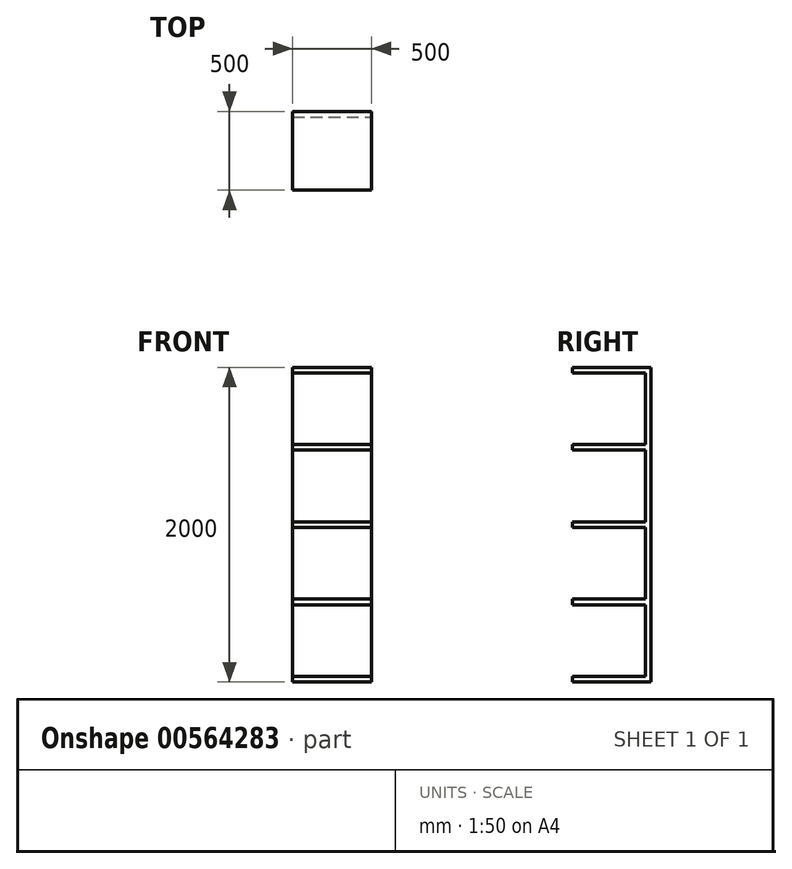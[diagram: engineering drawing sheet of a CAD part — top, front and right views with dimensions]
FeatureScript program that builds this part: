
annotation { "Feature Type Name" : "Feature", "Feature Type Description" : "" }
export const myFeature = defineFeature(function(context is Context, id is Id, definition is map)
    precondition{}
    {
        {
            var Q0;
            Q0=qCreatedBy(makeId("Front.planeOp"),FACE);
            var sketch = newSketch(context, id + "F0", { "sketchPlane" : qUnion([Q0])});
            skLineSegment(sketch, "E0.bottom", {"start": v(-253.9, 1006.9) * mm, "end": v(246.1, 1006.9) * mm});
            skLineSegment(sketch, "E0.top", {"start": v(-253.9, -993.1) * mm, "end": v(246.1, -993.1) * mm});
            skLineSegment(sketch, "E0.left", {"start": v(-253.9, 1006.9) * mm, "end": v(-253.9, -993.1) * mm});
            skLineSegment(sketch, "E0.right", {"start": v(246.1, 1006.9) * mm, "end": v(246.1, -993.1) * mm});
            skSolve(sketch);
        }
        {
            var Q0;
            Q0=makeQuery(id+"F0.imprint","IMPRINT",FACE,{"disambiguationData":[TD([[makeQuery(id+"F0.imprint","IMPRINT",EDGE,{"derivedFrom":sQuery(id+"F0.wireOp",EDGE,"E0.bottom")}),-1.0]])]});
            extrude(context, id + "F1", {"entities" : qUnion([Q0]), "depth" : 500 * mm, "offsetDistance" : 25 * mm});
        }
        {
            var Q0;
            Q0=makeQuery(id+"F1.opExtrude","CAP_FACE",FACE,{"disambiguationData":[OSD([sQuery(id+"F0.wireOp",EDGE,"E0.bottom"),sQuery(id+"F0.wireOp",EDGE,"E0.top"),sQuery(id+"F0.wireOp",EDGE,"E0.left"),sQuery(id+"F0.wireOp",EDGE,"E0.right")])],"isStart":false});
            var sketch = newSketch(context, id + "F2", { "sketchPlane" : qUnion([Q0])});
            skLineSegment(sketch, "E1.bottom", {"start": v(-253.9, 971.9) * mm, "end": v(246.1, 971.9) * mm});
            skLineSegment(sketch, "E1.top", {"start": v(-253.9, 515.9) * mm, "end": v(246.1, 515.9) * mm});
            skLineSegment(sketch, "E1.left", {"start": v(-253.9, 971.9) * mm, "end": v(-253.9, 515.9) * mm});
            skLineSegment(sketch, "E1.right", {"start": v(246.1, 971.9) * mm, "end": v(246.1, 515.9) * mm});
            skLineSegment(sketch, "E2.bottom", {"start": v(-253.9, 480.9) * mm, "end": v(246.1, 480.9) * mm});
            skLineSegment(sketch, "E2.top", {"start": v(-253.9, 24.9) * mm, "end": v(246.1, 24.9) * mm});
            skLineSegment(sketch, "E2.left", {"start": v(-253.9, 480.9) * mm, "end": v(-253.9, 24.9) * mm});
            skLineSegment(sketch, "E2.right", {"start": v(246.1, 480.9) * mm, "end": v(246.1, 24.9) * mm});
            skLineSegment(sketch, "E3.bottom", {"start": v(-253.9, -10.1) * mm, "end": v(246.1, -10.1) * mm});
            skLineSegment(sketch, "E3.top", {"start": v(-253.9, -466.1) * mm, "end": v(246.1, -466.1) * mm});
            skLineSegment(sketch, "E3.left", {"start": v(-253.9, -10.1) * mm, "end": v(-253.9, -466.1) * mm});
            skLineSegment(sketch, "E3.right", {"start": v(246.1, -10.1) * mm, "end": v(246.1, -466.1) * mm});
            skLineSegment(sketch, "E4.bottom", {"start": v(-253.9, -501.1) * mm, "end": v(246.1, -501.1) * mm});
            skLineSegment(sketch, "E4.top", {"start": v(-253.9, -958.1) * mm, "end": v(246.1, -958.1) * mm});
            skLineSegment(sketch, "E4.left", {"start": v(-253.9, -501.1) * mm, "end": v(-253.9, -958.1) * mm});
            skLineSegment(sketch, "E4.right", {"start": v(246.1, -501.1) * mm, "end": v(246.1, -958.1) * mm});
            skSolve(sketch);
        }
        {
            var Q0;
            Q0=makeQuery(id+"F2.imprint","IMPRINT",FACE,{"disambiguationData":[TD([[makeQuery(id+"F2.imprint","IMPRINT",EDGE,{"derivedFrom":sQuery(id+"F2.wireOp",EDGE,"E1.bottom")}),-1.0]])]});
            var Q1;
            Q1=makeQuery(id+"F2.imprint","IMPRINT",FACE,{"disambiguationData":[TD([[makeQuery(id+"F2.imprint","IMPRINT",EDGE,{"derivedFrom":sQuery(id+"F2.wireOp",EDGE,"E2.bottom")}),-1.0]])]});
            var Q2;
            Q2=makeQuery(id+"F2.imprint","IMPRINT",FACE,{"disambiguationData":[TD([[makeQuery(id+"F2.imprint","IMPRINT",EDGE,{"derivedFrom":sQuery(id+"F2.wireOp",EDGE,"E3.bottom")}),-1.0]])]});
            var Q3;
            Q3=makeQuery(id+"F2.imprint","IMPRINT",FACE,{"disambiguationData":[TD([[makeQuery(id+"F2.imprint","IMPRINT",EDGE,{"derivedFrom":sQuery(id+"F2.wireOp",EDGE,"E4.bottom")}),-1.0]])]});
            extrude(context, id + "F3", {"entities" : qUnion([Q0, Q1, Q2, Q3]), "operationType" : NewBodyOperationType.REMOVE, "oppositeDirection" : true, "depth" : 465 * mm, "offsetDistance" : 25 * mm});
        }
    });
